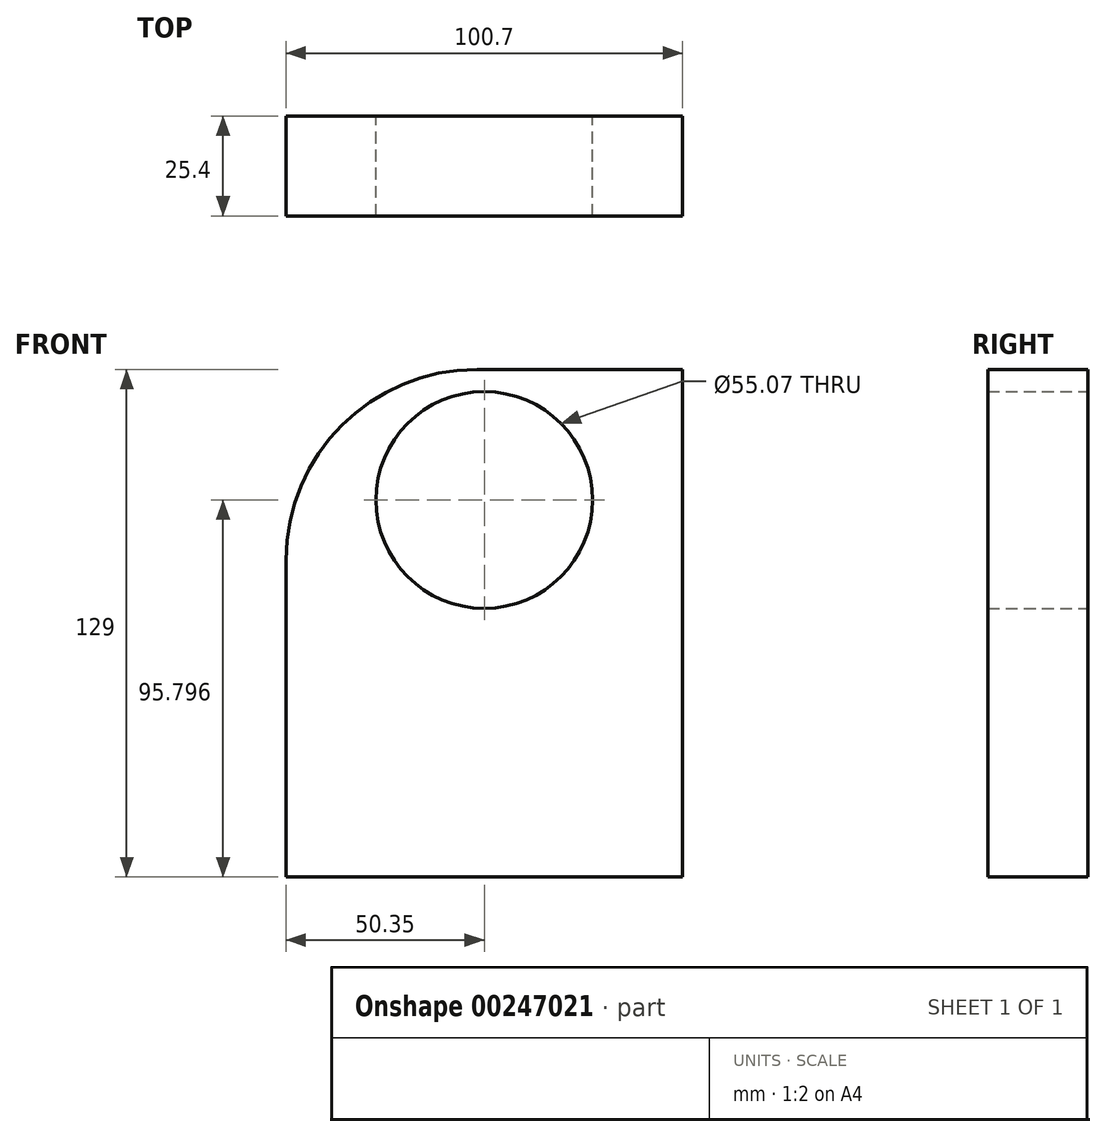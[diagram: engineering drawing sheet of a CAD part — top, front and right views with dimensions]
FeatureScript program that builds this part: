
annotation { "Feature Type Name" : "Feature", "Feature Type Description" : "" }
export const myFeature = defineFeature(function(context is Context, id is Id, definition is map)
    precondition{}
    {
        {
            var Q0;
            Q0=qCreatedBy(makeId("Front.planeOp"),FACE);
            var sketch = newSketch(context, id + "F0", { "sketchPlane" : qUnion([Q0])});
            skLineSegment(sketch, "E0.bottom", {"start": v(50.35, -64.5) * mm, "end": v(-50.35, -64.5) * mm});
            skLineSegment(sketch, "E0.top", {"start": v(50.35, 64.5) * mm, "end": v(-50.35, 64.5) * mm});
            skLineSegment(sketch, "E0.left", {"start": v(50.35, -64.5) * mm, "end": v(50.35, 64.5) * mm});
            skLineSegment(sketch, "E0.right", {"start": v(-50.35, -64.5) * mm, "end": v(-50.35, 64.5) * mm});
            skPoint(sketch, "E0.middle", {"position": v(0, 0) * mm});
            skSolve(sketch);
        }
        {
            var Q0;
            Q0=makeQuery(id+"F0.imprint","IMPRINT",FACE,{"disambiguationData":[TD([[makeQuery(id+"F0.imprint","IMPRINT",EDGE,{"derivedFrom":sQuery(id+"F0.wireOp",EDGE,"E0.bottom")}),-1.0]])]});
            extrude(context, id + "F1", {"entities" : qUnion([Q0]), "depth" : 25.4 * mm});
        }
        {
            var Q0;
            Q0=qCreatedBy(makeId("Front.planeOp"),FACE);
            var sketch = newSketch(context, id + "F2", { "sketchPlane" : qUnion([Q0])});
            skCircle(sketch, "E1", {"center": v(0, 31.3) * mm, "radius": 27.53 * mm});
            skSolve(sketch);
        }
        {
            var Q0;
            Q0=makeQuery(id+"F2.imprint","IMPRINT",FACE,{"disambiguationData":[TD([[makeQuery(id+"F2.imprint","IMPRINT",EDGE,{"derivedFrom":sQuery(id+"F2.wireOp",EDGE,"E1")}),1.0]])]});
            extrude(context, id + "F3", {"entities" : qUnion([Q0]), "operationType" : NewBodyOperationType.REMOVE, "depth" : 170.94 * mm});
        }
        {
            var Q0;
            Q0=makeQuery(id+"F1.opExtrude","SWEPT_EDGE",EDGE,{"disambiguationData":[OSD([sQuery(id+"F0.wireOp",EDGE,"E0.top"),sQuery(id+"F0.wireOp",EDGE,"E0.right")])]});
            fillet(context, id + "F4", {"entities" : qUnion([Q0]), "radius" : 48.44 * mm, "tangentPropagation" : true, "allowEdgeOverflow" : false});
        }
    });
